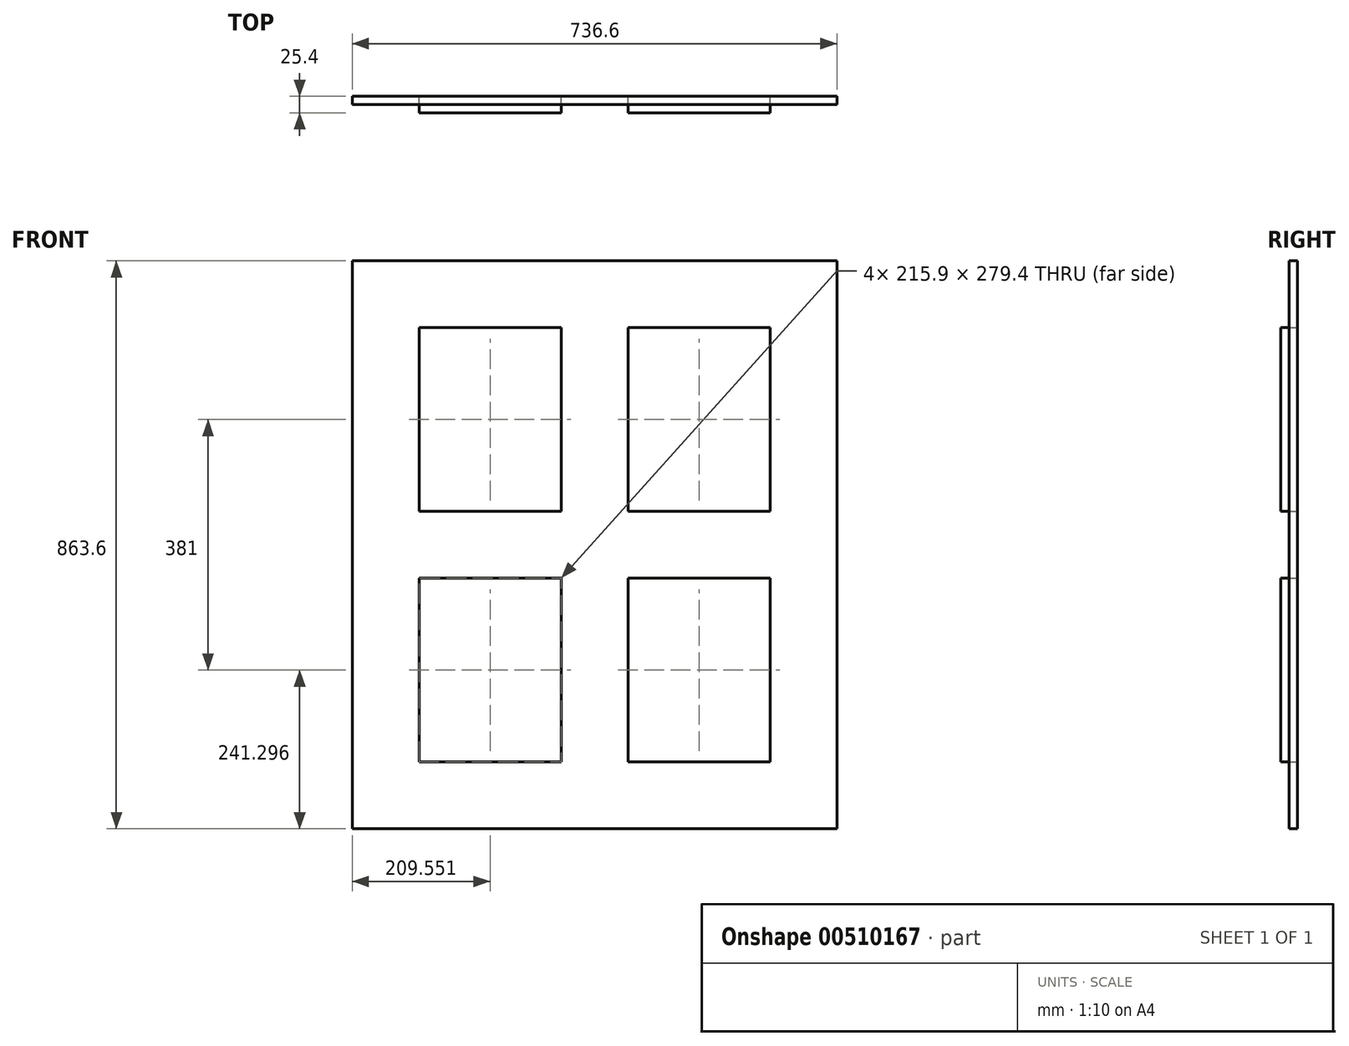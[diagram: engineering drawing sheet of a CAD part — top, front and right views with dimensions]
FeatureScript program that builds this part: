
annotation { "Feature Type Name" : "Feature", "Feature Type Description" : "" }
export const myFeature = defineFeature(function(context is Context, id is Id, definition is map)
    precondition{}
    {
        {
            var Q0;
            Q0=qCreatedBy(makeId("Front.planeOp"),FACE);
            var sketch = newSketch(context, id + "F0", { "sketchPlane" : qUnion([Q0])});
            skLineSegment(sketch, "E0.bottom", {"start": v(-324.07, 273.32) * mm, "end": v(-108.17, 273.32) * mm});
            skLineSegment(sketch, "E0.top", {"start": v(-324.07, -6.08) * mm, "end": v(-108.17, -6.08) * mm});
            skLineSegment(sketch, "E0.left", {"start": v(-324.07, 273.32) * mm, "end": v(-324.07, -6.08) * mm});
            skLineSegment(sketch, "E1", {"start": v(-108.17, 273.32) * mm, "end": v(-6.57, 273.27) * mm});
            skLineSegment(sketch, "E2", {"start": v(-6.57, 273.27) * mm, "end": v(-6.57, -6.13) * mm});
            skLineSegment(sketch, "E3", {"start": v(-6.57, 273.27) * mm, "end": v(209.33, 273.27) * mm});
            skLineSegment(sketch, "E4", {"start": v(209.33, 273.27) * mm, "end": v(209.33, -6.13) * mm});
            skLineSegment(sketch, "E5", {"start": v(209.33, -6.13) * mm, "end": v(-6.57, -6.13) * mm});
            skLineSegment(sketch, "E6", {"start": v(209.33, -6.13) * mm, "end": v(209.33, -107.73) * mm});
            skLineSegment(sketch, "E7", {"start": v(209.33, -107.73) * mm, "end": v(-6.57, -107.73) * mm});
            skLineSegment(sketch, "E8", {"start": v(-6.57, -107.73) * mm, "end": v(-6.57, -387.13) * mm});
            skLineSegment(sketch, "E9", {"start": v(-6.57, -387.13) * mm, "end": v(209.33, -387.13) * mm});
            skLineSegment(sketch, "E10", {"start": v(209.33, -387.13) * mm, "end": v(209.33, -107.73) * mm});
            skLineSegment(sketch, "E11", {"start": v(-324.07, -6.08) * mm, "end": v(-324.07, -107.68) * mm});
            skLineSegment(sketch, "E12", {"start": v(-324.07, -107.68) * mm, "end": v(-108.17, -107.68) * mm});
            skLineSegment(sketch, "E13", {"start": v(-108.17, -107.68) * mm, "end": v(-108.17, -387.08) * mm});
            skLineSegment(sketch, "E14", {"start": v(-108.17, -387.08) * mm, "end": v(-324.07, -387.08) * mm});
            skLineSegment(sketch, "E15", {"start": v(-324.07, -387.08) * mm, "end": v(-324.07, -107.68) * mm});
            skLineSegment(sketch, "E16", {"start": v(-108.17, 273.32) * mm, "end": v(-108.17, -6.08) * mm});
            skLineSegment(sketch, "E17", {"start": v(-324.07, 273.32) * mm, "end": v(-324.07, 374.92) * mm});
            skLineSegment(sketch, "E18", {"start": v(-324.07, 374.92) * mm, "end": v(-425.67, 374.92) * mm});
            skLineSegment(sketch, "E19.bottom", {"start": v(-425.67, 374.92) * mm, "end": v(310.93, 374.92) * mm});
            skLineSegment(sketch, "E19.top", {"start": v(-425.67, -488.68) * mm, "end": v(310.93, -488.68) * mm});
            skLineSegment(sketch, "E19.left", {"start": v(-425.67, 374.92) * mm, "end": v(-425.67, -488.68) * mm});
            skLineSegment(sketch, "E19.right", {"start": v(310.93, 374.92) * mm, "end": v(310.93, -488.68) * mm});
            skSolve(sketch);
        }
        {
            var Q0;
            Q0=makeQuery(id+"F0.imprint","IMPRINT",FACE,{"disambiguationData":[TD([[makeQuery(id+"F0.imprint","IMPRINT",EDGE,{"derivedFrom":sQuery(id+"F0.wireOp",EDGE,"E2")}),1.0]])]});
            var Q1;
            Q1=makeQuery(id+"F0.imprint","IMPRINT",FACE,{"disambiguationData":[TD([[makeQuery(id+"F0.imprint","IMPRINT",EDGE,{"derivedFrom":sQuery(id+"F0.wireOp",EDGE,"E0.bottom")}),-1.0]])]});
            var Q2;
            Q2=makeQuery(id+"F0.imprint","IMPRINT",FACE,{"disambiguationData":[TD([[makeQuery(id+"F0.imprint","IMPRINT",EDGE,{"derivedFrom":sQuery(id+"F0.wireOp",EDGE,"E12")}),-1.0]])]});
            var Q3;
            Q3=makeQuery(id+"F0.imprint","IMPRINT",FACE,{"disambiguationData":[TD([[makeQuery(id+"F0.imprint","IMPRINT",EDGE,{"derivedFrom":sQuery(id+"F0.wireOp",EDGE,"E7")}),1.0]])]});
            extrude(context, id + "F1", {"entities" : qUnion([Q0, Q1, Q2, Q3]), "depth" : 25.4 * mm});
        }
        {
            var Q0;
            Q0 = qSketchRegion(id + "F0", true);
            extrude(context, id + "F2", {"entities" : qUnion([Q0]), "depth" : 12.7 * mm});
        }
    });
